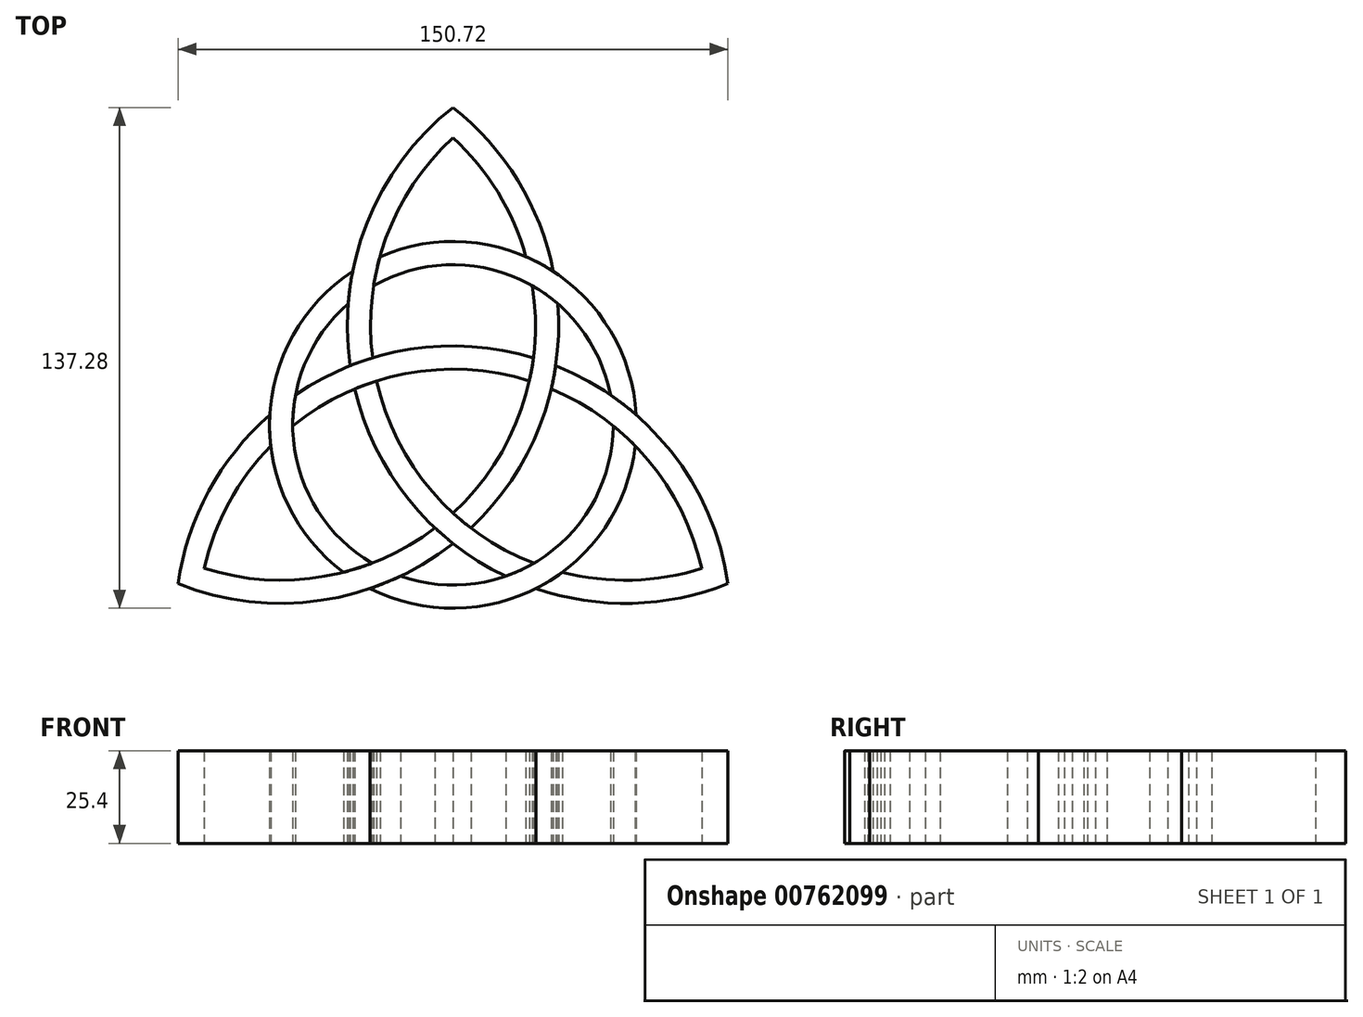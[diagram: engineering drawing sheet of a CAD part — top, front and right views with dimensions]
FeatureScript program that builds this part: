
annotation { "Feature Type Name" : "Feature", "Feature Type Description" : "" }
export const myFeature = defineFeature(function(context is Context, id is Id, definition is map)
    precondition{}
    {
        {
            var Q0;
            Q0=qCreatedBy(makeId("Top.planeOp"),FACE);
            var sketch = newSketch(context, id + "F0", { "sketchPlane" : qUnion([Q0])});
            skPoint(sketch, "E0", {"position": v(0, -43.9) * mm});
            skPoint(sketch, "E1", {"position": v(37.68, 21.76) * mm});
            skPoint(sketch, "E2", {"position": v(-37.68, 21.76) * mm});
            skArc(sketch, "E3", {"start": v(-75.36, -43.51) * mm, "mid": v(-36.2, -48.1) * mm, "end": v(0, -32.5) * mm});
            skArc(sketch, "E4", {"start": v(0, 87.02) * mm, "mid": v(-23.55, 55.4) * mm, "end": v(-28.14, 16.25) * mm});
            skArc(sketch, "E5", {"start": v(75.36, -43.51) * mm, "mid": v(59.76, -7.3) * mm, "end": v(28.14, 16.25) * mm});
            skArc(sketch, "E6.0", {"start": v(68.14, -39.34) * mm, "mid": v(53.53, -9.71) * mm, "end": v(26.93, 9.88) * mm});
            skArc(sketch, "E7.0", {"start": v(-68.14, -39.34) * mm, "mid": v(-35.18, -41.5) * mm, "end": v(-4.9, -28.26) * mm});
            skArc(sketch, "E8.0", {"start": v(0, 78.68) * mm, "mid": v(-18.35, 51.21) * mm, "end": v(-22.02, 18.38) * mm});
            skArc(sketch, "E9", {"start": v(-27.49, 42.07) * mm, "mid": v(-50.24, 1.49) * mm, "end": v(-29.93, -40.37) * mm});
            skArc(sketch, "E10.0", {"start": v(-28.7, 33.22) * mm, "mid": v(-43.72, -4.02) * mm, "end": v(-22.17, -37.9) * mm});
            skArc(sketch, "E11.trimOffspring", {"start": v(20, 46.1) * mm, "mid": v(12.27, 63.8) * mm, "end": v(0, 78.68) * mm});
            skArc(sketch, "E12.trimOffspring", {"start": v(27.49, 42.07) * mm, "mid": v(17.75, 67) * mm, "end": v(0, 87.02) * mm});
            skArc(sketch, "E13.trimOffspring", {"start": v(-50.18, 2.77) * mm, "mid": v(-66.9, -18.12) * mm, "end": v(-75.36, -43.51) * mm});
            skArc(sketch, "E14.trimOffspring", {"start": v(-49.93, -5.73) * mm, "mid": v(-61.38, -21.27) * mm, "end": v(-68.14, -39.34) * mm});
            skArc(sketch, "E15.trimOffspring", {"start": v(-14.42, -41.47) * mm, "mid": v(25.34, -35.85) * mm, "end": v(43.9, -0.25) * mm});
            skArc(sketch, "E16.trimOffspring", {"start": v(-22.7, -44.84) * mm, "mid": v(23.83, -44.25) * mm, "end": v(49.93, -5.73) * mm});
            skArc(sketch, "E17.trimOffspring", {"start": v(22.7, -44.84) * mm, "mid": v(49.15, -48.88) * mm, "end": v(75.36, -43.51) * mm});
            skArc(sketch, "E18.trimOffspring", {"start": v(29.93, -40.37) * mm, "mid": v(49.1, -42.52) * mm, "end": v(68.14, -39.34) * mm});
            skArc(sketch, "E19.trimOffspring", {"start": v(50.18, 2.77) * mm, "mid": v(26.4, 42.76) * mm, "end": v(-20, 46.1) * mm});
            skArc(sketch, "E20.trimOffspring", {"start": v(43.12, 8.25) * mm, "mid": v(18.38, 39.87) * mm, "end": v(-21.74, 38.15) * mm});
            skArc(sketch, "E21.trimOffspring", {"start": v(-26.93, 9.88) * mm, "mid": v(-12.1, -20.5) * mm, "end": v(14.42, -41.47) * mm});
            skArc(sketch, "E22.trimOffspring", {"start": v(-20.92, 12.08) * mm, "mid": v(-5.65, -18.32) * mm, "end": v(22.17, -37.9) * mm});
            skArc(sketch, "E23.trimOffspring", {"start": v(0, -24.16) * mm, "mid": v(18.7, 4.27) * mm, "end": v(21.74, 38.15) * mm});
            skArc(sketch, "E24.trimOffspring", {"start": v(4.9, -28.26) * mm, "mid": v(23.8, -0.23) * mm, "end": v(28.7, 33.22) * mm});
            skArc(sketch, "E25.trimOffspring", {"start": v(22.02, 18.38) * mm, "mid": v(-11.7, 20.73) * mm, "end": v(-43.12, 8.25) * mm});
            skArc(sketch, "E26.trimOffspring", {"start": v(20.92, 12.08) * mm, "mid": v(-13.04, 14.06) * mm, "end": v(-43.9, -0.25) * mm});
            skSolve(sketch);
        }
        {
            var Q0;
            {var subQ0=sQuery(id+"F0.wireOp",EDGE,"E11.trimOffspring");Q0=makeQuery(id+"F0.imprint","IMPRINT",FACE,{"disambiguationData":[TD([[makeQuery(id+"F0.imprint","IMPRINT",EDGE,{"derivedFrom":subQ0}),-1.0]])]});}
            extrude(context, id + "F1", {"entities" : qUnion([Q0]), "depth" : 25.4 * mm, "offsetDistance" : 25.4 * mm});
        }
        {
            var Q0;
            {var subQ0=sQuery(id+"F0.wireOp",EDGE,"E21.trimOffspring");var subQ5=sQuery(id+"F0.wireOp",EDGE,"E15.trimOffspring");var subQ6=makeQuery(id+"F0.imprint","INTERSECT",VERTEX,{"derivedFrom":[subQ5,subQ0]});Q0=makeQuery(id+"F0.imprint","IMPRINT",FACE,{"disambiguationData":[TD([[makeQuery(id+"F0.imprint","IMPRINT",EDGE,{"disambiguationData":[TD([[subQ6,-1.0]])],"derivedFrom":subQ5}),1.0]])]});}
            extrude(context, id + "F2", {"entities" : qUnion([Q0]), "depth" : 25.4 * mm, "offsetDistance" : 25.4 * mm});
        }
        {
            var Q0;
            {var subQ10=sQuery(id+"F0.wireOp",EDGE,"E17.trimOffspring");Q0=makeQuery(id+"F0.imprint","IMPRINT",FACE,{"disambiguationData":[TD([[makeQuery(id+"F0.imprint","IMPRINT",EDGE,{"derivedFrom":subQ10}),1.0]])]});}
            extrude(context, id + "F3", {"entities" : qUnion([Q0]), "depth" : 25.4 * mm, "offsetDistance" : 25.4 * mm});
        }
        {
            var Q0;
            {var subQ0=sQuery(id+"F0.wireOp",EDGE,"E25.trimOffspring");var subQ3=sQuery(id+"F0.wireOp",EDGE,"E10.0");var subQ4=makeQuery(id+"F0.imprint","INTERSECT",VERTEX,{"derivedFrom":[subQ3,subQ0]});Q0=makeQuery(id+"F0.imprint","IMPRINT",FACE,{"disambiguationData":[TD([[makeQuery(id+"F0.imprint","IMPRINT",EDGE,{"disambiguationData":[TD([[subQ4,-1.0]])],"derivedFrom":subQ3}),1.0]])]});}
            extrude(context, id + "F4", {"entities" : qUnion([Q0]), "depth" : 25.4 * mm, "offsetDistance" : 25.4 * mm});
        }
        {
            var Q0;
            {var subQ10=sQuery(id+"F0.wireOp",EDGE,"E13.trimOffspring");Q0=makeQuery(id+"F0.imprint","IMPRINT",FACE,{"disambiguationData":[TD([[makeQuery(id+"F0.imprint","IMPRINT",EDGE,{"derivedFrom":subQ10}),1.0]])]});}
            extrude(context, id + "F5", {"entities" : qUnion([Q0]), "depth" : 25.4 * mm, "offsetDistance" : 25.4 * mm});
        }
        {
            var Q0;
            {var subQ0=sQuery(id+"F0.wireOp",EDGE,"E23.trimOffspring");var subQ7=sQuery(id+"F0.wireOp",EDGE,"E20.trimOffspring");var subQ8=makeQuery(id+"F0.imprint","INTERSECT",VERTEX,{"derivedFrom":[subQ7,subQ0]});Q0=makeQuery(id+"F0.imprint","IMPRINT",FACE,{"disambiguationData":[TD([[makeQuery(id+"F0.imprint","IMPRINT",EDGE,{"disambiguationData":[TD([[subQ8,1.0]])],"derivedFrom":subQ7}),1.0]])]});}
            extrude(context, id + "F6", {"entities" : qUnion([Q0]), "depth" : 25.4 * mm, "offsetDistance" : 25.4 * mm});
        }
        {
            var Q0;
            {var subQ0=sQuery(id+"F0.wireOp",EDGE,"E19.trimOffspring");var subQ2=sQuery(id+"F0.wireOp",EDGE,"E5");var subQ3=makeQuery(id+"F0.imprint","INTERSECT",VERTEX,{"derivedFrom":[subQ2,subQ0]});Q0=makeQuery(id+"F0.imprint","IMPRINT",FACE,{"disambiguationData":[TD([[makeQuery(id+"F0.imprint","IMPRINT",EDGE,{"disambiguationData":[TD([[subQ3,-1.0]])],"derivedFrom":subQ2}),-1.0]])]});}
            extrude(context, id + "F7", {"entities" : qUnion([Q0]), "depth" : 25.4 * mm, "offsetDistance" : 25.4 * mm});
        }
        {
            var Q0;
            {var subQ0=sQuery(id+"F0.wireOp",EDGE,"E9");var subQ1=sQuery(id+"F0.wireOp",EDGE,"E4");var subQ2=makeQuery(id+"F0.imprint","INTERSECT",VERTEX,{"derivedFrom":[subQ1,subQ0]});Q0=makeQuery(id+"F0.imprint","IMPRINT",FACE,{"disambiguationData":[TD([[makeQuery(id+"F0.imprint","IMPRINT",EDGE,{"disambiguationData":[TD([[subQ2,-1.0]])],"derivedFrom":subQ1}),-1.0]])]});}
            extrude(context, id + "F8", {"entities" : qUnion([Q0]), "depth" : 25.4 * mm, "offsetDistance" : 25.4 * mm});
        }
        {
            var Q0;
            {var subQ0=sQuery(id+"F0.wireOp",EDGE,"E15.trimOffspring");var subQ3=sQuery(id+"F0.wireOp",EDGE,"E3");var subQ4=makeQuery(id+"F0.imprint","INTERSECT",VERTEX,{"derivedFrom":[subQ3,subQ0]});Q0=makeQuery(id+"F0.imprint","IMPRINT",FACE,{"disambiguationData":[TD([[makeQuery(id+"F0.imprint","IMPRINT",EDGE,{"disambiguationData":[TD([[subQ4,1.0]])],"derivedFrom":subQ3}),-1.0]])]});}
            extrude(context, id + "F9", {"entities" : qUnion([Q0]), "depth" : 25.4 * mm, "offsetDistance" : 25.4 * mm});
        }
    });
